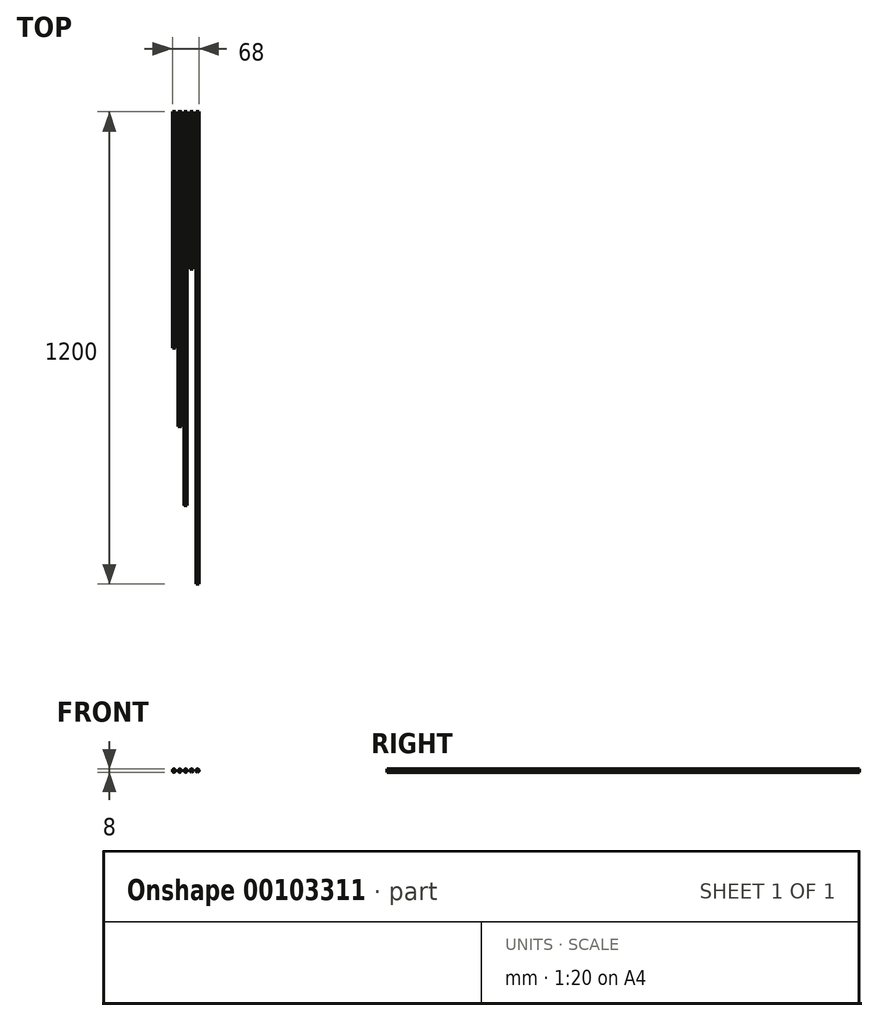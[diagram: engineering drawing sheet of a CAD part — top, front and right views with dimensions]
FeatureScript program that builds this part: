
annotation { "Feature Type Name" : "Feature", "Feature Type Description" : "" }
export const myFeature = defineFeature(function(context is Context, id is Id, definition is map)
    precondition{}
    {
        {
            var Q0;
            Q0=qCreatedBy(makeId("Front.planeOp"),FACE);
            var sketch = newSketch(context, id + "F0", { "sketchPlane" : qUnion([Q0])});
            skCircle(sketch, "E0", {"center": v(0, 0) * mm, "radius": 4 * mm});
            skCircle(sketch, "E1", {"center": v(15, 0) * mm, "radius": 4 * mm});
            skCircle(sketch, "E2", {"center": v(30, 0) * mm, "radius": 4 * mm});
            skCircle(sketch, "E3", {"center": v(-15, 0) * mm, "radius": 4 * mm});
            skCircle(sketch, "E4", {"center": v(-30, 0) * mm, "radius": 4 * mm});
            skSolve(sketch);
        }
        {
            var Q0;
            Q0=makeQuery(id+"F0.imprint","IMPRINT",FACE,{"disambiguationData":[TD([[makeQuery(id+"F0.imprint","IMPRINT",EDGE,{"derivedFrom":sQuery(id+"F0.wireOp",EDGE,"E0")}),1.0]])]});
            extrude(context, id + "F1", {"entities" : qUnion([Q0]), "depth" : 1000 * mm});
        }
        {
            var Q0;
            Q0=makeQuery(id+"F0.imprint","IMPRINT",FACE,{"disambiguationData":[TD([[makeQuery(id+"F0.imprint","IMPRINT",EDGE,{"derivedFrom":sQuery(id+"F0.wireOp",EDGE,"E3")}),1.0]])]});
            var Q1;
            Q1=sQuery(id+"F0.wireOp",EDGE,"E3");
            extrude(context, id + "F2", {"entities" : qUnion([Q0]), "surfaceEntities" : qUnion([Q1]), "depth" : 800 * mm});
        }
        {
            var Q0;
            Q0=makeQuery(id+"F0.imprint","IMPRINT",FACE,{"disambiguationData":[TD([[makeQuery(id+"F0.imprint","IMPRINT",EDGE,{"derivedFrom":sQuery(id+"F0.wireOp",EDGE,"E4")}),1.0]])]});
            extrude(context, id + "F3", {"entities" : qUnion([Q0]), "depth" : 600 * mm});
        }
        {
            var Q0;
            Q0=makeQuery(id+"F0.imprint","IMPRINT",FACE,{"disambiguationData":[TD([[makeQuery(id+"F0.imprint","IMPRINT",EDGE,{"derivedFrom":sQuery(id+"F0.wireOp",EDGE,"E1")}),1.0]])]});
            var Q1;
            Q1 = qConstructionFilter(qBodyType(qCreatedBy(id + "F0" ,EDGE), BodyType.WIRE), ConstructionObject.NO);
            extrude(context, id + "F4", {"entities" : qUnion([Q0]), "surfaceEntities" : qUnion([Q1]), "depth" : 400 * mm});
        }
        {
            var Q0;
            Q0=makeQuery(id+"F0.imprint","IMPRINT",FACE,{"disambiguationData":[TD([[makeQuery(id+"F0.imprint","IMPRINT",EDGE,{"derivedFrom":sQuery(id+"F0.wireOp",EDGE,"E2")}),1.0]])]});
            extrude(context, id + "F5", {"entities" : qUnion([Q0]), "depth" : 1200 * mm});
        }
    });
